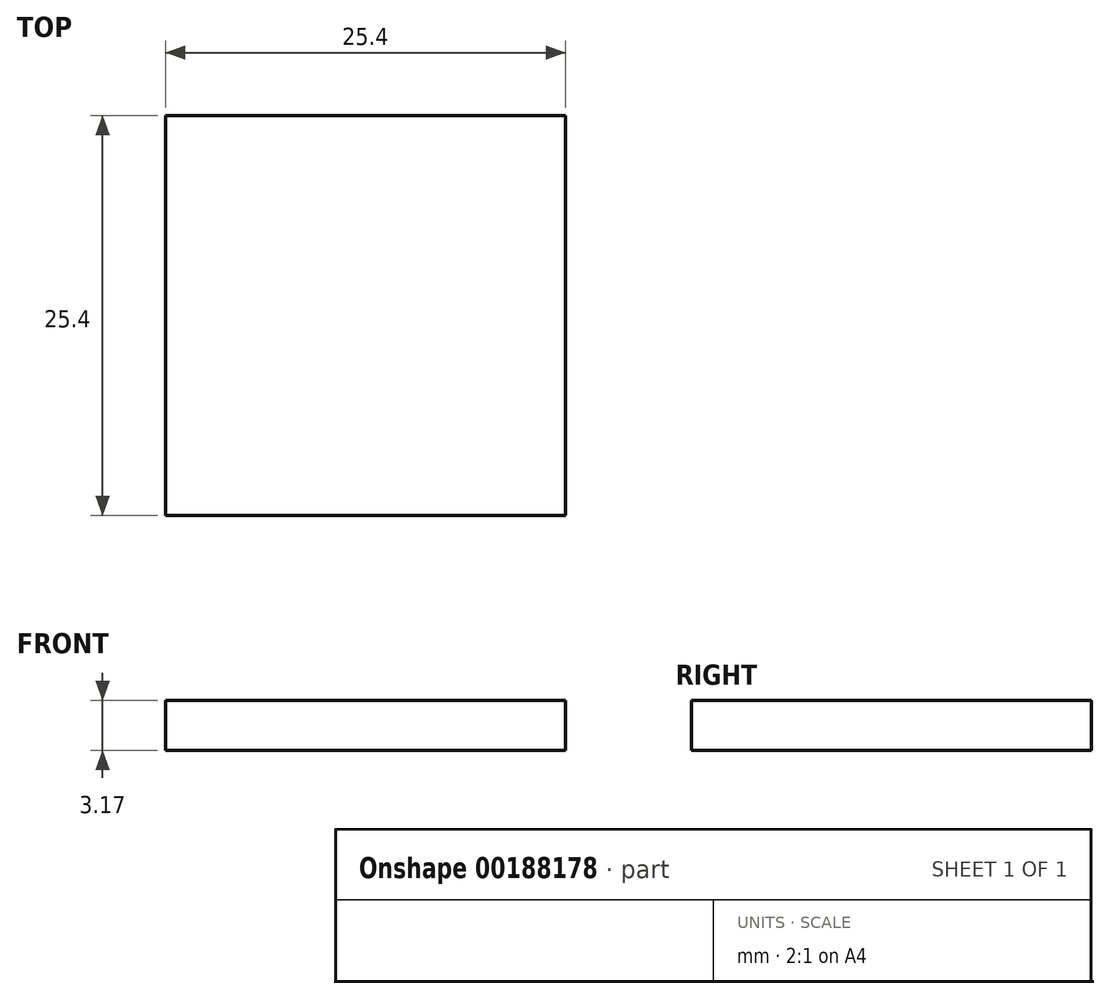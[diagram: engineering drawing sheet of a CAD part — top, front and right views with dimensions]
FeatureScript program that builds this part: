
annotation { "Feature Type Name" : "Feature", "Feature Type Description" : "" }
export const myFeature = defineFeature(function(context is Context, id is Id, definition is map)
    precondition{}
    {
        {
            var Q0;
            Q0=qCreatedBy(makeId("Top.planeOp"),FACE);
            var sketch = newSketch(context, id + "F0", { "sketchPlane" : qUnion([Q0])});
            skLineSegment(sketch, "E0.bottom", {"start": v(12.7, 12.7) * mm, "end": v(-12.7, 12.7) * mm});
            skLineSegment(sketch, "E0.top", {"start": v(12.7, -12.7) * mm, "end": v(-12.7, -12.7) * mm});
            skLineSegment(sketch, "E0.left", {"start": v(12.7, 12.7) * mm, "end": v(12.7, -12.7) * mm});
            skLineSegment(sketch, "E0.right", {"start": v(-12.7, 12.7) * mm, "end": v(-12.7, -12.7) * mm});
            skPoint(sketch, "E0.middle", {"position": v(0, 0) * mm});
            skSolve(sketch);
        }
        {
            var Q0;
            Q0 = qSketchRegion(id + "F0", true);
            extrude(context, id + "F1", {"entities" : qUnion([Q0]), "depth" : 3.17 * mm});
        }
    });
